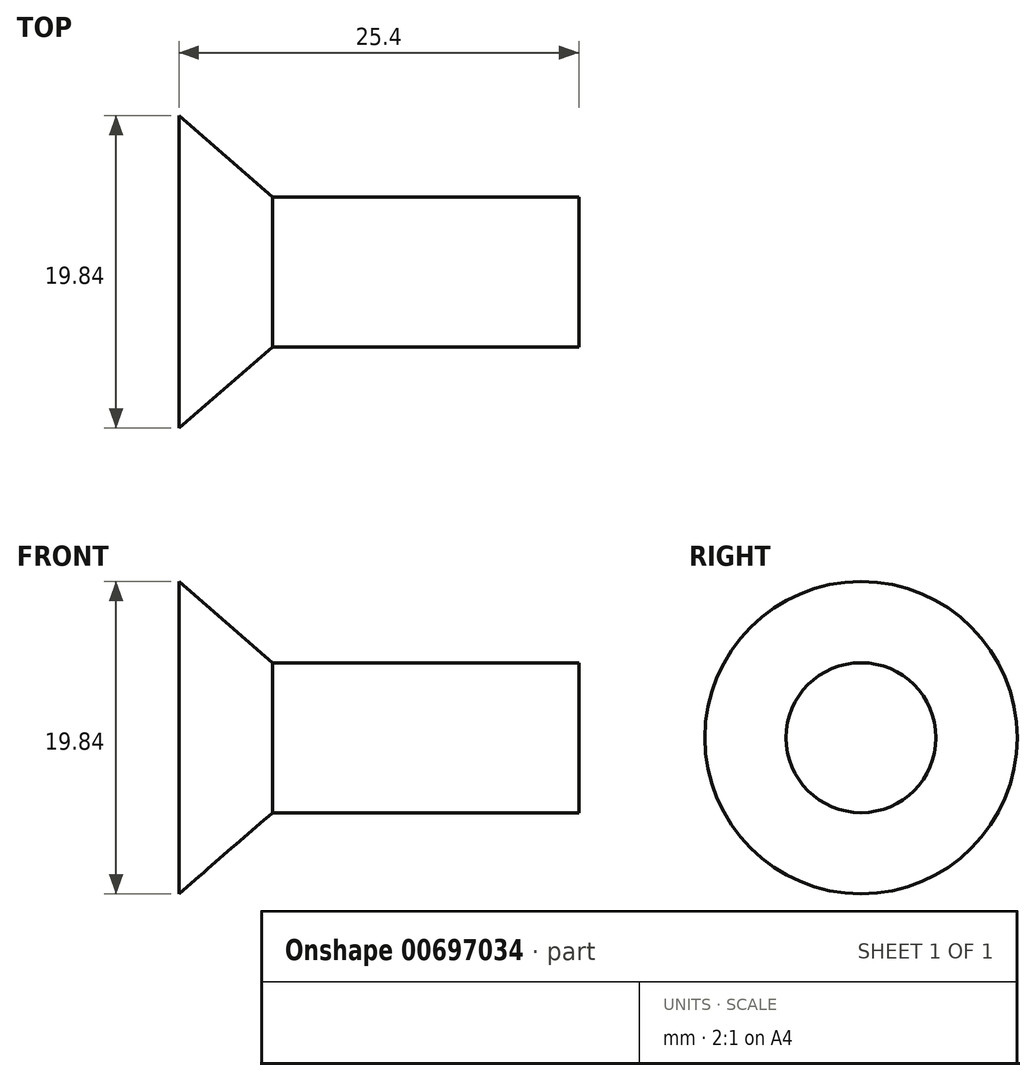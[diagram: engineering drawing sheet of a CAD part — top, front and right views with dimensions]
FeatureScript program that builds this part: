
annotation { "Feature Type Name" : "Feature", "Feature Type Description" : "" }
export const myFeature = defineFeature(function(context is Context, id is Id, definition is map)
    precondition{}
    {
        {
            var Q0;
            Q0=qCreatedBy(makeId("Front.planeOp"),FACE);
            var sketch = newSketch(context, id + "F0", { "sketchPlane" : qUnion([Q0])});
            skLineSegment(sketch, "E0", {"start": v(94.93, 0) * mm, "end": v(-113.96, 0) * mm, "construction": true});
            skLineSegment(sketch, "E1", {"start": v(-24.81, 0) * mm, "end": v(-24.81, 9.92) * mm});
            skLineSegment(sketch, "E2", {"start": v(-24.81, 9.92) * mm, "end": v(-18.88, 4.76) * mm});
            skLineSegment(sketch, "E3", {"start": v(-18.88, 4.76) * mm, "end": v(0.59, 4.76) * mm});
            skLineSegment(sketch, "E4", {"start": v(0.59, 4.76) * mm, "end": v(0.59, 0) * mm});
            skLineSegment(sketch, "E5", {"start": v(0.59, 0) * mm, "end": v(-24.81, 0) * mm});
            skSolve(sketch);
        }
        {
            var Q0;
            Q0 = qSketchRegion(id + "F0", true);
            var Q1;
            Q1=sQuery(id+"F0.wireOp",EDGE,"E0");
            revolve(context, id + "F1", {"entities" : qUnion([Q0]), "axis" : qUnion([Q1]), "revolveType" : RevolveType.FULL});
        }
    });
